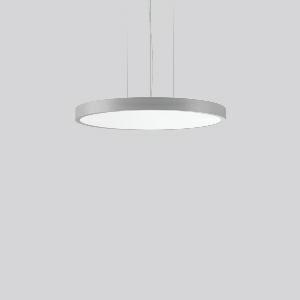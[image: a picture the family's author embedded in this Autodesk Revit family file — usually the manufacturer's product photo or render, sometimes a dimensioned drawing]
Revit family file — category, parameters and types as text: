
# Revit family: triona_round_p_312385_004_76_1253
name_source: partatom
category: Lighting Fixtures
units: mm (PartAtom-declared; Revit-internal decimal feet)

## family parameters
Cut with Voids When Loaded = No
Host = Face
Light Source = No
Part Type = Normal
Room Calculation Point = No
Round Connector Dimension = Use Diameter
Shared = No

## types (1)
- TRIONA round P (1 x LED Modul 830, 6450 lm, 3000)
    Apparent Load = 70 VA
    CIE Flux Codes = 49 80 96 100 100
    Color Rendering = 80
    Color Temperature = 3000
    Default Elevation = 1800 mm
    Description = Series: TRIONA round
Decorative round LED pendant-mounted surface luminaire. Flat, seamless frame: aluminium extrusion profile, powder coated. Cover made of sheet steel, powder-coated. Canopy made of aluminium, powder-coated. Light emission through a diffuser: plastic, opal. Lightguide and diffuser made of non-yellowing plastic (PMMA). Lateral light emission (RZB SIDELITE technology) for above-average homogeneous light distribution. 3-point steel cable suspension, steplessly adjustable. Easy installation with transparent, adjustable pendant cable and canopy with magnetic fixing. Driver integrated. 
Colour: silver, matt (approx. RAL 9006)
Diameter: 681 mm
Height: 52 mm
Suspension length: 500-1200 mm
Lamp: LED
Socket: without socket
Colour temperature: 3000K
Colour rendering index (CRI): 80
System power: 70 W
Rated luminous flux: 6450 lm
Luminous efficiency: 92 lm/W
Control gear: Converter, dimmable, DALI
Protection class: I
Type of protection: IP 20
    Height = 52 mm
    Lamp = 1 x LED Modul 830
    Lamp Light Flux = 6450 lm
    Lamp count = 1
    Length = 681 mm
    Lifetime = 50000 h
    Luminous efficacy = 92 lm/W
    Manufacturer = RZB
    ModVariant = No
    Model = 312385.004.76
    Mounting Place = Ceiling
    Mounting Type = Pendant
    Number of Poles = 1
    OnlyDefault = Yes
    Power Factor = 1
    Product Name = TRIONA round P
    Product group = Pendant modular luminaires
    ProductGroupID = 906
    Protection Class = Protection class I
    Protection Degree = IP 20
    RLX_Detail_Level = 1
    RLX_Emergency_Light_Flux = 0 lm
    RLX_Emergency_Type = 0
    RLX_Emergency_Type_DB = No
    RlxData = <blob elided: 27857 chars, md5=af1617fa>
    Socket = socket
    Standby Power = 0 W
    System Light Flux = 6450 lm
    System Power = 70 W
    Type Comments = Product without accessories
    Type Image = 312386.004.jpg
    URL = http://relux.com
    VarID = ---
    Voltage = 230 V
    Voltage Range = 220-240 V
    Weight = 0.00 kg
    Width = 0 mm  [stored 0 ft]

note: [stored X ft] marks values corroborated as IEEE doubles in the binary element streams (Revit-internal decimal feet)

## geometry (parser evidence)
native form markers: Blend x4, Sweep x12
no freeform markers — native parametric forms only
